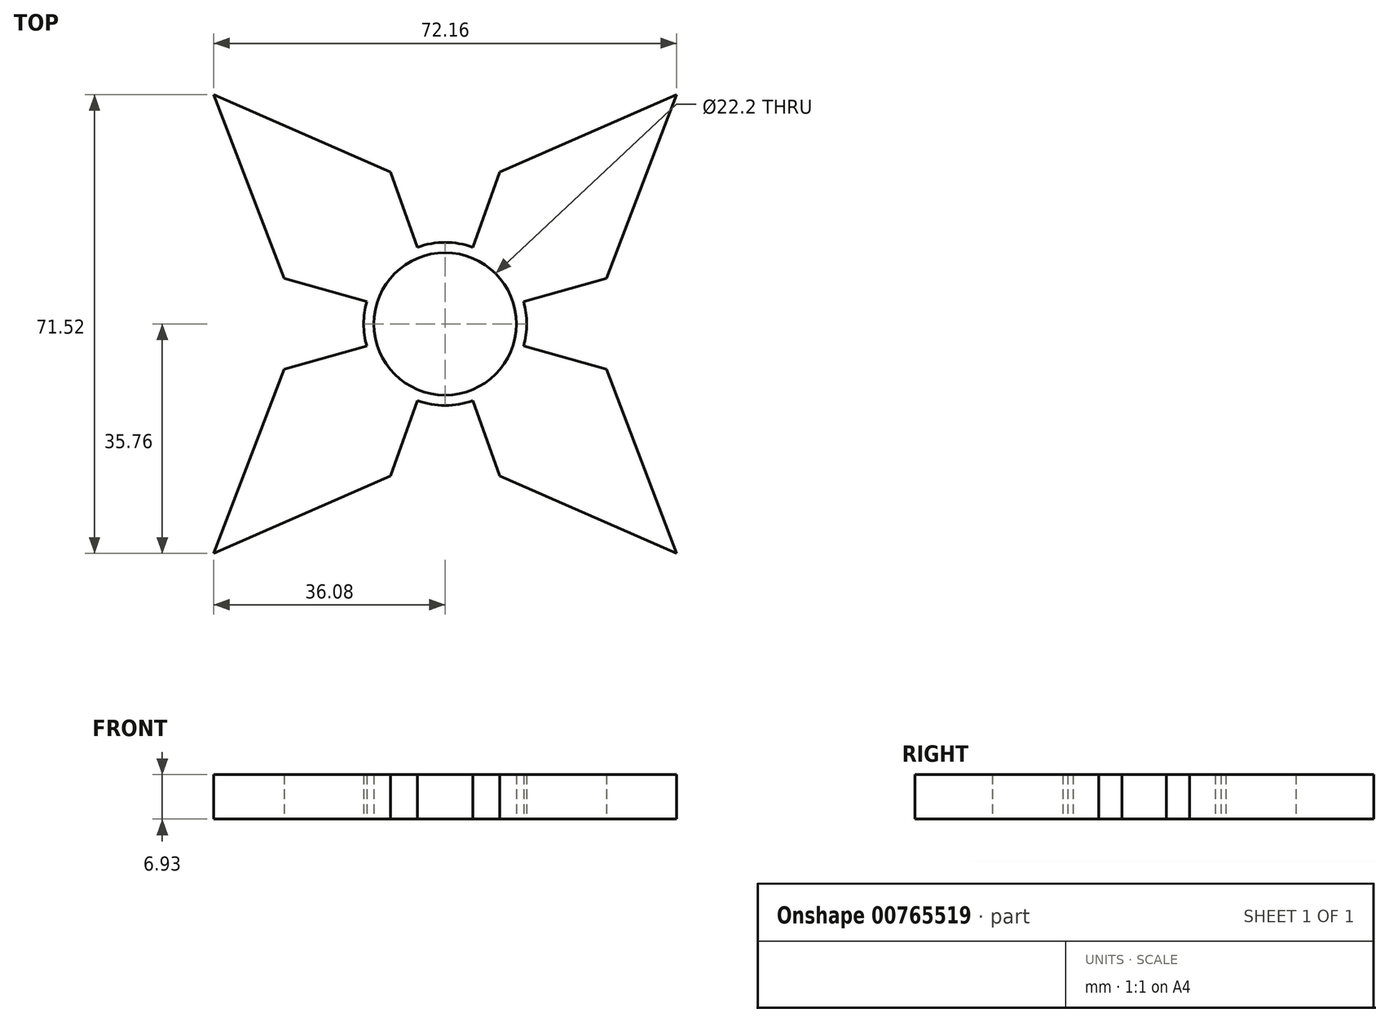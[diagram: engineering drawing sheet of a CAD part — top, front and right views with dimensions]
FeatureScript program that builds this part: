
annotation { "Feature Type Name" : "Feature", "Feature Type Description" : "" }
export const myFeature = defineFeature(function(context is Context, id is Id, definition is map)
    precondition{}
    {
        {
            var Q0;
            Q0=qCreatedBy(makeId("Top.planeOp"),FACE);
            var sketch = newSketch(context, id + "F0", { "sketchPlane" : qUnion([Q0])});
            skLineSegment(sketch, "E0", {"start": v(-10.68, 3.01) * mm, "end": v(-25.12, 7.09) * mm});
            skLineSegment(sketch, "E1", {"start": v(-25.12, 7.09) * mm, "end": v(-36.08, 35.76) * mm});
            skLineSegment(sketch, "E2", {"start": v(-36.08, 35.76) * mm, "end": v(-8.53, 23.67) * mm});
            skLineSegment(sketch, "E3", {"start": v(-8.53, 23.67) * mm, "end": v(-3.76, 10.44) * mm});
            skLineSegment(sketch, "E4.MirrorCS", {"start": v(8.53, 23.67) * mm, "end": v(3.76, 10.44) * mm});
            skLineSegment(sketch, "E5.MirrorCS", {"start": v(36.08, 35.76) * mm, "end": v(8.53, 23.67) * mm});
            skLineSegment(sketch, "E6.MirrorCS", {"start": v(25.12, 7.09) * mm, "end": v(36.08, 35.76) * mm});
            skLineSegment(sketch, "E7.MirrorCS", {"start": v(10.68, 3.01) * mm, "end": v(25.12, 7.09) * mm});
            skLineSegment(sketch, "E8.MirrorCS", {"start": v(25.12, -7.09) * mm, "end": v(36.08, -35.76) * mm});
            skLineSegment(sketch, "E9.MirrorCS", {"start": v(36.08, -35.76) * mm, "end": v(8.53, -23.67) * mm});
            skLineSegment(sketch, "E10.MirrorCS", {"start": v(8.53, -23.67) * mm, "end": v(3.76, -10.44) * mm});
            skLineSegment(sketch, "E11.MirrorCS", {"start": v(10.68, -3.01) * mm, "end": v(25.12, -7.09) * mm});
            skLineSegment(sketch, "E12.MirrorCS", {"start": v(-8.53, -23.67) * mm, "end": v(-3.76, -10.44) * mm});
            skLineSegment(sketch, "E13.MirrorCS", {"start": v(-10.68, -3.01) * mm, "end": v(-25.12, -7.09) * mm});
            skLineSegment(sketch, "E14.MirrorCS", {"start": v(-25.12, -7.09) * mm, "end": v(-36.08, -35.76) * mm});
            skLineSegment(sketch, "E15.MirrorCS", {"start": v(-36.08, -35.76) * mm, "end": v(-8.53, -23.67) * mm});
            skCircle(sketch, "E16", {"center": v(0, 0) * mm, "radius": 11.1 * mm});
            skCircle(sketch, "E17", {"center": v(0, 0) * mm, "radius": 12.7 * mm});
            skLineSegment(sketch, "E18", {"start": v(-36.08, 35.76) * mm, "end": v(-9.27, 8.68) * mm});
            skSolve(sketch);
        }
        {
            var Q0;
            Q0 = qSketchRegion(id + "F0", true);
            extrude(context, id + "F1", {"entities" : qUnion([Q0]), "depth" : 6.93 * mm, "offsetDistance" : 25.4 * mm});
        }
    });
